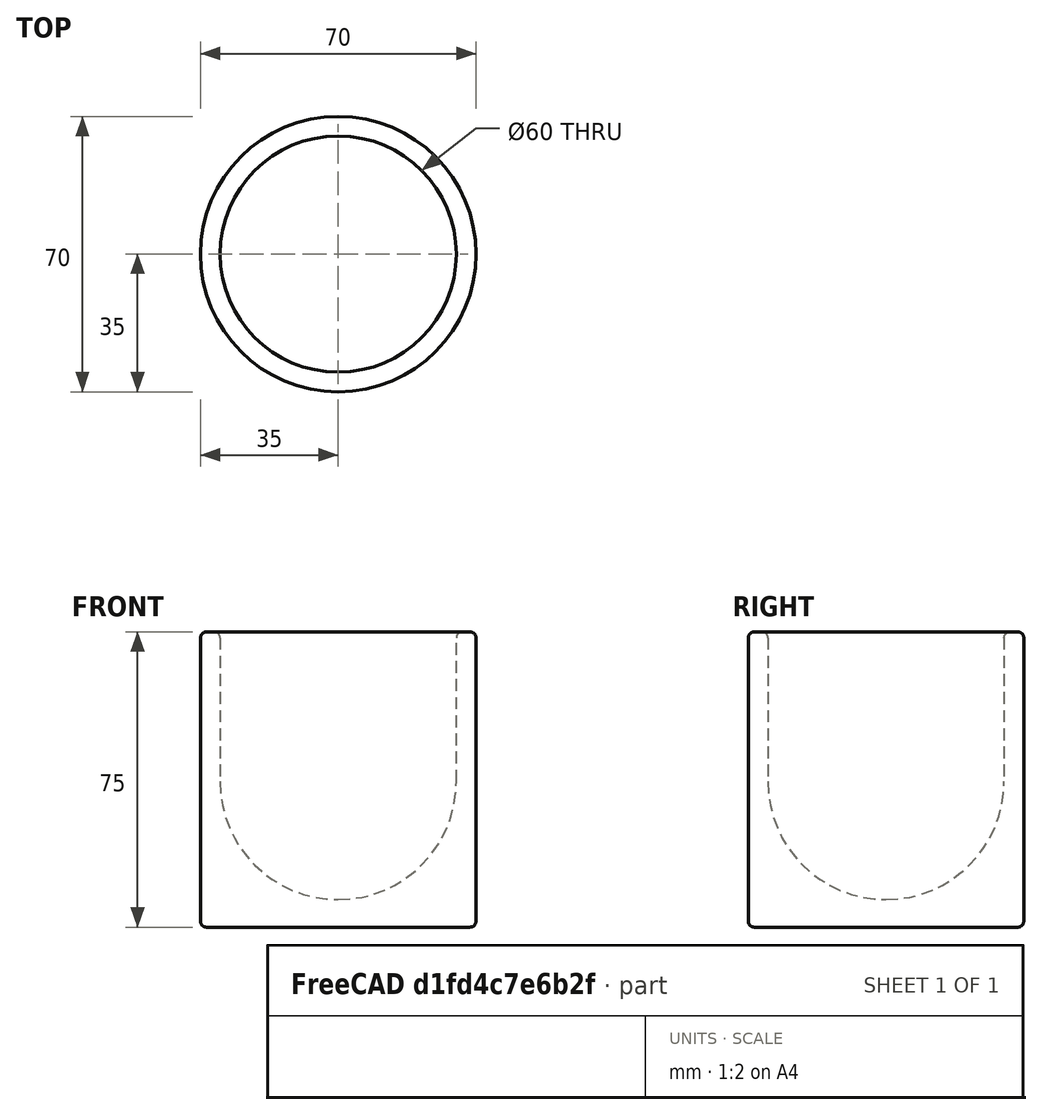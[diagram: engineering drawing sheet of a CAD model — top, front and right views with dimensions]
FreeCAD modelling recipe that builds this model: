
FCSTD DOCUMENT  (FreeCAD 1.0R1.0.0)
Label: Crucible_Cylinder_5mmwall_rounded
License: All rights reserved
LicenseURL: http://en.wikipedia.org/wiki/All_rights_reserved
objects: Part::Cylinder×2, Part::Sphere×1, Part::MultiFuse×1, Part::Cut×1, Part::Fillet×1
note: 6 computed .brp shape members not serialized (recipe doc carries the construction recipe); baked Part::Feature solids carry a one-line shape summary decoded from their .brp

FEATURE [Part::Cylinder] Cylinder
  Angle = 360
  AttacherType = Attacher::AttachEngine3D
  FirstAngle = 0
  Height = 75
  Radius = 35
  SecondAngle = 0
FEATURE [Part::Sphere] Sphere
  Angle1 = -90
  Angle2 = 90
  Angle3 = 360
  AttacherType = Attacher::AttachEngine3D
  Placement = pos=(0,0,37) rot=(0,0,1;0rad)
  Radius = 30
FEATURE [Part::Cylinder] Cylinder001
  Angle = 360
  AttacherType = Attacher::AttachEngine3D
  FirstAngle = 0
  Height = 75
  Placement = pos=(0,0,37) rot=(0,0,1;0rad)
  Radius = 30
  SecondAngle = 0
FEATURE [Part::MultiFuse] Fusion
  Shapes = -> [Sphere,Cylinder001]
FEATURE [Part::Cut] Cut
  Base = -> Cylinder
  Tool = -> Fusion
FEATURE [Part::Fillet] Fillet
  Base = -> Cut
  EdgeLinks = -> Cut [Edge2,Edge3,Edge4]
  Edges = 3 edges r=1.5: [Edge2,Edge3,Edge4]
